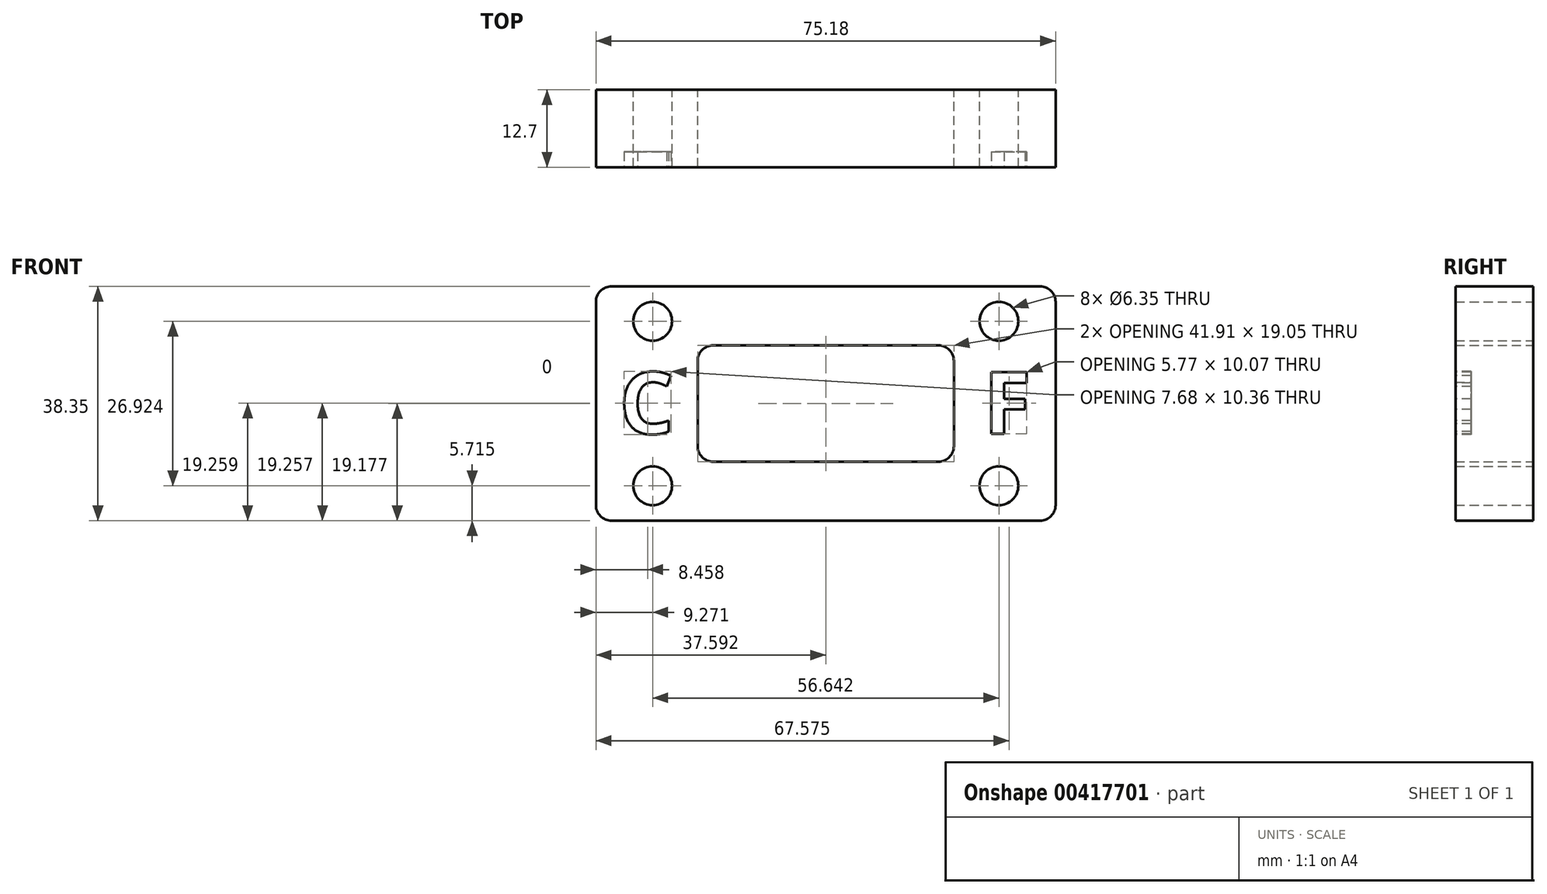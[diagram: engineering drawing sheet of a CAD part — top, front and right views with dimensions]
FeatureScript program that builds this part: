
annotation { "Feature Type Name" : "Feature", "Feature Type Description" : "" }
export const myFeature = defineFeature(function(context is Context, id is Id, definition is map)
    precondition{}
    {
        {
            var Q0;
            Q0=qCreatedBy(makeId("Front.planeOp"),FACE);
            var sketch = newSketch(context, id + "F0", { "sketchPlane" : qUnion([Q0])});
            skLineSegment(sketch, "E0.bottom", {"start": v(0, 0) * mm, "end": v(75.18, 0) * mm});
            skLineSegment(sketch, "E0.top", {"start": v(0, 38.35) * mm, "end": v(75.18, 38.35) * mm});
            skLineSegment(sketch, "E0.left", {"start": v(0, 0) * mm, "end": v(0, 38.35) * mm});
            skLineSegment(sketch, "E0.right", {"start": v(75.18, 0) * mm, "end": v(75.18, 38.35) * mm});
            skCircle(sketch, "E1", {"center": v(9.27, 32.64) * mm, "radius": 3.18 * mm});
            skCircle(sketch, "E2", {"center": v(9.27, 5.72) * mm, "radius": 3.18 * mm});
            skCircle(sketch, "E3", {"center": v(65.91, 32.64) * mm, "radius": 3.18 * mm});
            skCircle(sketch, "E4", {"center": v(65.91, 5.72) * mm, "radius": 3.18 * mm});
            skLineSegment(sketch, "E5.bottom", {"start": v(16.64, 9.65) * mm, "end": v(58.55, 9.65) * mm});
            skLineSegment(sketch, "E5.top", {"start": v(16.64, 28.7) * mm, "end": v(58.55, 28.7) * mm});
            skLineSegment(sketch, "E5.left", {"start": v(16.64, 9.65) * mm, "end": v(16.64, 28.7) * mm});
            skLineSegment(sketch, "E5.right", {"start": v(58.55, 9.65) * mm, "end": v(58.55, 28.7) * mm});
            skSolve(sketch);
        }
        {
            var Q0;
            Q0 = qSketchRegion(id + "F0", true);
            extrude(context, id + "F1", {"entities" : qUnion([Q0]), "depth" : 12.7 * mm});
        }
        {
            var Q0;
            Q0=makeQuery(id+"F1.opExtrude","SWEPT_EDGE",EDGE,{"disambiguationData":[OSD([sQuery(id+"F0.wireOp",EDGE,"E0.top"),sQuery(id+"F0.wireOp",EDGE,"E0.left")])]});
            var Q1;
            Q1=makeQuery(id+"F1.opExtrude","SWEPT_EDGE",EDGE,{"disambiguationData":[OSD([sQuery(id+"F0.wireOp",EDGE,"E0.bottom"),sQuery(id+"F0.wireOp",EDGE,"E0.left")])]});
            var Q2;
            Q2=makeQuery(id+"F1.opExtrude","SWEPT_EDGE",EDGE,{"disambiguationData":[OSD([sQuery(id+"F0.wireOp",EDGE,"E0.top"),sQuery(id+"F0.wireOp",EDGE,"E0.right")])]});
            var Q3;
            Q3=makeQuery(id+"F1.opExtrude","SWEPT_EDGE",EDGE,{"disambiguationData":[OSD([sQuery(id+"F0.wireOp",EDGE,"E0.bottom"),sQuery(id+"F0.wireOp",EDGE,"E0.right")])]});
            var Q4;
            Q4=makeQuery(id+"F1.opExtrude","SWEPT_EDGE",EDGE,{"disambiguationData":[OSD([sQuery(id+"F0.wireOp",EDGE,"E5.top"),sQuery(id+"F0.wireOp",EDGE,"E5.left")])]});
            var Q5;
            Q5=makeQuery(id+"F1.opExtrude","SWEPT_EDGE",EDGE,{"disambiguationData":[OSD([sQuery(id+"F0.wireOp",EDGE,"E5.bottom"),sQuery(id+"F0.wireOp",EDGE,"E5.right")])]});
            var Q6;
            Q6=makeQuery(id+"F1.opExtrude","SWEPT_EDGE",EDGE,{"disambiguationData":[OSD([sQuery(id+"F0.wireOp",EDGE,"E5.top"),sQuery(id+"F0.wireOp",EDGE,"E5.right")])]});
            var Q7;
            Q7=makeQuery(id+"F1.opExtrude","SWEPT_EDGE",EDGE,{"disambiguationData":[OSD([sQuery(id+"F0.wireOp",EDGE,"E5.bottom"),sQuery(id+"F0.wireOp",EDGE,"E5.left")])]});
            fillet(context, id + "F2", {"entities" : qUnion([Q0, Q1, Q2, Q3, Q4, Q5, Q6, Q7]), "radius" : 2.54 * mm, "tangentPropagation" : true, "allowEdgeOverflow" : false});
        }
        {
            var Q0;
            Q0=makeQuery(id+"F1.opExtrude","CAP_FACE",FACE,{"disambiguationData":[OSD([sQuery(id+"F0.wireOp",EDGE,"E0.bottom"),sQuery(id+"F0.wireOp",EDGE,"E0.top"),sQuery(id+"F0.wireOp",EDGE,"E0.left"),sQuery(id+"F0.wireOp",EDGE,"E0.right"),sQuery(id+"F0.wireOp",EDGE,"E1"),sQuery(id+"F0.wireOp",EDGE,"E2"),sQuery(id+"F0.wireOp",EDGE,"E3"),sQuery(id+"F0.wireOp",EDGE,"E4"),sQuery(id+"F0.wireOp",EDGE,"E5.bottom"),sQuery(id+"F0.wireOp",EDGE,"E5.top"),sQuery(id+"F0.wireOp",EDGE,"E5.left"),sQuery(id+"F0.wireOp",EDGE,"E5.right")])],"isStart":false});
            var sketch = newSketch(context, id + "F3", { "sketchPlane" : qUnion([Q0])});
            skText(sketch, "E6", { "text": "C", "fontName": "OpenSans-Bold.ttf"});
            skText(sketch, "E7", { "text": "F", "fontName": "OpenSans-Bold.ttf"});
            const initialGuessF3  = {"E6": [0.0038, 0.01422, 1, 0, 0.01016], "E7": [0.06342, 0.01422, 1, 0, 0.01016]};
            skSetInitialGuess(sketch, initialGuessF3);
            skSolve(sketch);
        }
        {
            var Q0;
            Q0 = qSketchRegion(id + "F3", true);
            extrude(context, id + "F4", {"entities" : qUnion([Q0]), "operationType" : NewBodyOperationType.REMOVE, "oppositeDirection" : true, "depth" : 2.54 * mm});
        }
    });
